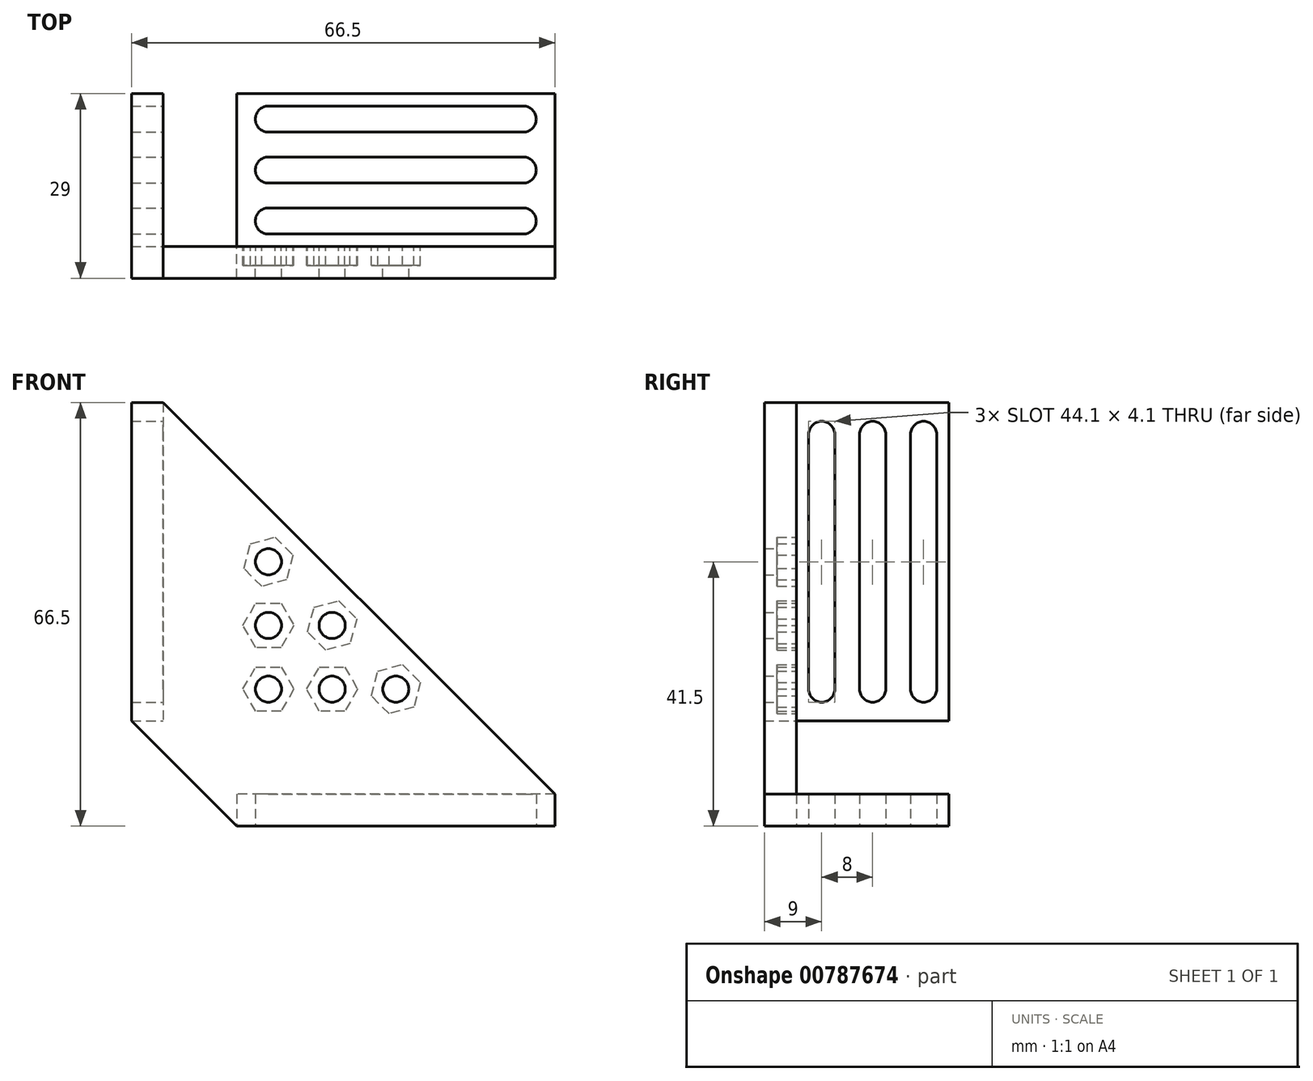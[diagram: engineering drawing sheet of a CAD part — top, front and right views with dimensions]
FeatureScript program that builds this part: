
annotation { "Feature Type Name" : "Feature", "Feature Type Description" : "" }
export const myFeature = defineFeature(function(context is Context, id is Id, definition is map)
    precondition{}
    {
        {
            var Q0;
            Q0=qCreatedBy(makeId("Top.planeOp"),FACE);
            var sketch = newSketch(context, id + "F0", { "sketchPlane" : qUnion([Q0])});
            skLineSegment(sketch, "E0.left", {"start": v(-21, 12) * mm, "end": v(-21, -12) * mm});
            skPoint(sketch, "E0.middle", {"position": v(0, 0) * mm});
            skLineSegment(sketch, "E1", {"start": v(-16, 12) * mm, "end": v(-16, -12) * mm, "construction": true});
            skPoint(sketch, "E2", {"position": v(-16, -8) * mm});
            skPoint(sketch, "E3", {"position": v(0, -8) * mm});
            skPoint(sketch, "E4", {"position": v(-16, 0) * mm});
            skArc(sketch, "E5", {"start": v(-16, -5.95) * mm, "mid": v(-18.05, -8) * mm, "end": v(-16, -10.05) * mm});
            skLineSegment(sketch, "E6", {"start": v(-16, -5.95) * mm, "end": v(0, -5.95) * mm});
            skLineSegment(sketch, "E7.MirrorCS", {"start": v(-16, -10.05) * mm, "end": v(0, -10.05) * mm});
            skArc(sketch, "E8", {"start": v(-16, -2.05) * mm, "mid": v(-18.05, 0) * mm, "end": v(-16, 2.05) * mm});
            skLineSegment(sketch, "E9", {"start": v(-16, -2.05) * mm, "end": v(0, -2.05) * mm});
            skPoint(sketch, "E10.MirrorP", {"position": v(-16, 2.05) * mm});
            skLineSegment(sketch, "E11.MirrorCS", {"start": v(-16, 2.05) * mm, "end": v(0, 2.05) * mm});
            skLineSegment(sketch, "E12.MirrorCS", {"start": v(0, -12) * mm, "end": v(0, 12) * mm, "construction": true});
            skLineSegment(sketch, "E13", {"start": v(-21, -12) * mm, "end": v(0, -12) * mm});
            skLineSegment(sketch, "E14", {"start": v(-21, 0) * mm, "end": v(0, 0) * mm, "construction": true});
            skLineSegment(sketch, "E15", {"start": v(0, -8) * mm, "end": v(-21, -8) * mm, "construction": true});
            skPoint(sketch, "E15.endSnap0", {"position": v(-18.05, -8) * mm});
            skLineSegment(sketch, "E16", {"start": v(0, -12) * mm, "end": v(29, -12) * mm});
            skLineSegment(sketch, "E17", {"start": v(29, -12) * mm, "end": v(29, 12) * mm});
            skLineSegment(sketch, "E18", {"start": v(29, 12) * mm, "end": v(-21, 12) * mm});
            skLineSegment(sketch, "E19", {"start": v(24, 12) * mm, "end": v(24, -12) * mm, "construction": true});
            skLineSegment(sketch, "E20", {"start": v(0, -5.95) * mm, "end": v(24, -5.95) * mm});
            skLineSegment(sketch, "E21", {"start": v(0, -10.05) * mm, "end": v(24, -10.05) * mm});
            skLineSegment(sketch, "E22", {"start": v(0, -2.05) * mm, "end": v(24, -2.05) * mm});
            skLineSegment(sketch, "E23", {"start": v(0, 2.05) * mm, "end": v(24, 2.05) * mm});
            skLineSegment(sketch, "E24", {"start": v(24, 0) * mm, "end": v(0, 0) * mm, "construction": true});
            skLineSegment(sketch, "E25", {"start": v(0, -8) * mm, "end": v(24, -8) * mm, "construction": true});
            skArc(sketch, "E26", {"start": v(24, -2.05) * mm, "mid": v(26.05, 0) * mm, "end": v(24, 2.05) * mm});
            skArc(sketch, "E27", {"start": v(24, -10.05) * mm, "mid": v(26.05, -8) * mm, "end": v(24, -5.95) * mm});
            skLineSegment(sketch, "E28.MirrorCS", {"start": v(0, 5.95) * mm, "end": v(24, 5.95) * mm});
            skLineSegment(sketch, "E29.MirrorCS", {"start": v(0, 10.05) * mm, "end": v(24, 10.05) * mm});
            skLineSegment(sketch, "E30.MirrorCS", {"start": v(-16, 10.05) * mm, "end": v(0, 10.05) * mm});
            skLineSegment(sketch, "E31.MirrorCS", {"start": v(-16, 5.95) * mm, "end": v(0, 5.95) * mm});
            skArc(sketch, "E32.MirrorCS", {"start": v(-16, 5.95) * mm, "mid": v(-18.05, 8) * mm, "end": v(-16, 10.05) * mm});
            skArc(sketch, "E33.MirrorCS", {"start": v(24, 10.05) * mm, "mid": v(26.05, 8) * mm, "end": v(24, 5.95) * mm});
            skSolve(sketch);
        }
        {
            var Q0;
            Q0=makeQuery(id+"F0.imprint","IMPRINT",FACE,{"disambiguationData":[TD([[makeQuery(id+"F0.imprint","IMPRINT",EDGE,{"derivedFrom":sQuery(id+"F0.wireOp",EDGE,"E0.bottom")}),-1.0]])]});
            var Q1;
            Q1=makeQuery(id+"F0.imprint","IMPRINT",FACE,{"disambiguationData":[TD([[makeQuery(id+"F0.imprint","IMPRINT",EDGE,{"derivedFrom":sQuery(id+"F0.wireOp",EDGE,"E0.left")}),1.0]])]});
            extrude(context, id + "F1", {"entities" : qUnion([Q0, Q1]), "depth" : 5 * mm, "offsetDistance" : 25 * mm});
        }
        {
            var Q0;
            Q0=makeQuery(id+"F1.opExtrude","SWEPT_FACE",FACE,{"disambiguationData":[OSD([sQuery(id+"F0.wireOp",EDGE,"E0.left")])]});
            var sketch = newSketch(context, id + "F2", { "sketchPlane" : qUnion([Q0])});
            skLineSegment(sketch, "E34", {"start": v(-12, 2.5) * mm, "end": v(12, 2.5) * mm, "construction": true});
            skSolve(sketch);
        }
        {
            var Q0;
            Q0=makeQuery(id+"F1.opExtrude","SWEPT_BODY",BODY,{"disambiguationData":[OSD([sQuery(id+"F0.wireOp",EDGE,"E0.bottom"),sQuery(id+"F0.wireOp",EDGE,"E0.top"),sQuery(id+"F0.wireOp",EDGE,"E0.left"),sQuery(id+"F0.wireOp",EDGE,"E0.right"),sQuery(id+"F0.wireOp",EDGE,"rf366HtQ-3S43-huQP-rZQL-GLvETnePYKPt"),sQuery(id+"F0.wireOp",EDGE,"72d57c59-205e-4b86-9b7f-fefa83471a3c0.MirrorC"),sQuery(id+"F0.wireOp",EDGE,"3BxVGwLA-TLUy-tZVP-cH0U-NxRYkcQ5ksQi"),sQuery(id+"F0.wireOp",EDGE,"b526d6a5-a937-4610-9a53-f8e406b30c9d0.MirrorC"),sQuery(id+"F0.wireOp",EDGE,"71981b63-6e51-433c-862b-60b74b25135c0.MirrorC"),sQuery(id+"F0.wireOp",EDGE,"b5f8f83e-67df-48da-9f18-6f8bbd20fa1b0.MirrorC"),sQuery(id+"F0.wireOp",EDGE,"1DxgEhBs-8iCY-IMLj-HmtB-05ri525AO9wY"),sQuery(id+"F0.wireOp",EDGE,"NxLUD5A4-VjtB-lD8M-x3iM-VxBEk0lLSaKk"),sQuery(id+"F0.wireOp",EDGE,"3f1f5e11-1e70-4af8-87df-d7b5c765f6460.MirrorC")])]});
            var Q1;
            Q1=sQuery(id+"F2.wireOp",EDGE,"E34");
            transform(context, id + "F3", {"entities" : qUnion([Q0]), "transformType" : TransformType.ROTATION, "transformAxis" : qUnion([Q1]), "angle" : 90 * degree, "makeCopy" : true});
        }
        {
            var Q0;
            Q0=makeQuery(id+"F3.opPattern","COPY",BODY,{"derivedFrom":makeQuery(id+"F1.opExtrude","SWEPT_BODY",BODY,{"disambiguationData":[OSD([sQuery(id+"F0.wireOp",EDGE,"E0.bottom"),sQuery(id+"F0.wireOp",EDGE,"E0.top"),sQuery(id+"F0.wireOp",EDGE,"E0.left"),sQuery(id+"F0.wireOp",EDGE,"E0.right"),sQuery(id+"F0.wireOp",EDGE,"rf366HtQ-3S43-huQP-rZQL-GLvETnePYKPt"),sQuery(id+"F0.wireOp",EDGE,"72d57c59-205e-4b86-9b7f-fefa83471a3c0.MirrorC"),sQuery(id+"F0.wireOp",EDGE,"3BxVGwLA-TLUy-tZVP-cH0U-NxRYkcQ5ksQi"),sQuery(id+"F0.wireOp",EDGE,"b526d6a5-a937-4610-9a53-f8e406b30c9d0.MirrorC"),sQuery(id+"F0.wireOp",EDGE,"71981b63-6e51-433c-862b-60b74b25135c0.MirrorC"),sQuery(id+"F0.wireOp",EDGE,"b5f8f83e-67df-48da-9f18-6f8bbd20fa1b0.MirrorC"),sQuery(id+"F0.wireOp",EDGE,"1DxgEhBs-8iCY-IMLj-HmtB-05ri525AO9wY"),sQuery(id+"F0.wireOp",EDGE,"NxLUD5A4-VjtB-lD8M-x3iM-VxBEk0lLSaKk"),sQuery(id+"F0.wireOp",EDGE,"3f1f5e11-1e70-4af8-87df-d7b5c765f6460.MirrorC")])]}),"instanceName":"1"});
            var Q1;
            Q1=qCreatedBy(makeId("Top.planeOp"),FACE);
            transform(context, id + "F4", {"entities" : qUnion([Q0]), "transformType" : TransformType.TRANSLATION_DISTANCE, "transformDirection" : qUnion([Q1]), "distance" : 14 * mm, "makeCopy" : false});
        }
        {
            var Q0;
            Q0=makeQuery(id+"F3.opPattern","COPY",BODY,{"derivedFrom":makeQuery(id+"F1.opExtrude","SWEPT_BODY",BODY,{"disambiguationData":[OSD([sQuery(id+"F0.wireOp",EDGE,"E0.bottom"),sQuery(id+"F0.wireOp",EDGE,"E0.top"),sQuery(id+"F0.wireOp",EDGE,"E0.left"),sQuery(id+"F0.wireOp",EDGE,"E0.right"),sQuery(id+"F0.wireOp",EDGE,"rf366HtQ-3S43-huQP-rZQL-GLvETnePYKPt"),sQuery(id+"F0.wireOp",EDGE,"72d57c59-205e-4b86-9b7f-fefa83471a3c0.MirrorC"),sQuery(id+"F0.wireOp",EDGE,"3BxVGwLA-TLUy-tZVP-cH0U-NxRYkcQ5ksQi"),sQuery(id+"F0.wireOp",EDGE,"b526d6a5-a937-4610-9a53-f8e406b30c9d0.MirrorC"),sQuery(id+"F0.wireOp",EDGE,"71981b63-6e51-433c-862b-60b74b25135c0.MirrorC"),sQuery(id+"F0.wireOp",EDGE,"b5f8f83e-67df-48da-9f18-6f8bbd20fa1b0.MirrorC"),sQuery(id+"F0.wireOp",EDGE,"1DxgEhBs-8iCY-IMLj-HmtB-05ri525AO9wY"),sQuery(id+"F0.wireOp",EDGE,"NxLUD5A4-VjtB-lD8M-x3iM-VxBEk0lLSaKk"),sQuery(id+"F0.wireOp",EDGE,"3f1f5e11-1e70-4af8-87df-d7b5c765f6460.MirrorC")])]}),"instanceName":"1"});
            var Q1;
            Q1=qCreatedBy(makeId("Right.planeOp"),FACE);
            transform(context, id + "F5", {"entities" : qUnion([Q0]), "transformType" : TransformType.TRANSLATION_DISTANCE, "transformDirection" : qUnion([Q1]), "distance" : 14 * mm, "oppositeDirection" : true, "makeCopy" : false});
        }
        {
            var Q0;
            Q0=makeQuery(id+"F3.opPattern","COPY",VERTEX,{"derivedFrom":makeQuery(id+"F1.opExtrude","CAP_VERTEX",VERTEX,{"disambiguationData":[OSD([sQuery(id+"F0.wireOp",EDGE,"E0.left"),sQuery(id+"F0.wireOp",EDGE,"E13")])],"isStart":false}),"instanceName":"1"});
            var Q1;
            Q1=makeQuery(id+"F3.opPattern","COPY",VERTEX,{"derivedFrom":makeQuery(id+"F1.opExtrude","CAP_VERTEX",VERTEX,{"disambiguationData":[OSD([sQuery(id+"F0.wireOp",EDGE,"E0.left"),sQuery(id+"F0.wireOp",EDGE,"E13")])],"isStart":true}),"instanceName":"1"});
            var Q2;
            Q2=sQuery(id+"F0.wireOp",VERTEX,"E0.left.end");
            cPlane(context, id + "F6", {"entities" : qUnion([Q0, Q1, Q2]), "cplaneType" : CPlaneType.THREE_POINT, "offset" : 25 * mm, "width" : 150 * mm, "height" : 150 * mm});
        }
        {
            var Q0;
            Q0=qCreatedBy(id+"F6.planeOp",FACE);
            var sketch = newSketch(context, id + "F7", { "sketchPlane" : qUnion([Q0])});
            skLineSegment(sketch, "E35", {"start": v(-21, 0) * mm, "end": v(-37.5, 16.5) * mm});
            skLineSegment(sketch, "E36", {"start": v(-32.5, 66.5) * mm, "end": v(29, 5) * mm});
            skLineSegment(sketch, "E37", {"start": v(-37.5, 16.5) * mm, "end": v(-37.5, 66.5) * mm});
            skLineSegment(sketch, "E38", {"start": v(-37.5, 66.5) * mm, "end": v(-32.5, 66.5) * mm});
            skLineSegment(sketch, "E39", {"start": v(-21, 0) * mm, "end": v(29, 0) * mm});
            skLineSegment(sketch, "E40", {"start": v(29, 0) * mm, "end": v(29, 5) * mm});
            skLineSegment(sketch, "E41", {"start": v(-32.5, 66.5) * mm, "end": v(-37.5, 66.5) * mm});
            skPoint(sketch, "E42", {"position": v(-6, 31.5) * mm});
            skCircle(sketch, "E43", {"center": v(-6, 31.5) * mm, "radius": 2.05 * mm});
            skCircle(sketch, "E44.cCircle", {"center": v(-6, 31.5) * mm, "radius": 4 * mm, "construction": true});
            skLineSegment(sketch, "E44.0", {"start": v(-8.82, 34.34) * mm, "end": v(-4.96, 35.37) * mm});
            skLineSegment(sketch, "E44.1", {"start": v(-4.96, 35.37) * mm, "end": v(-2.13, 32.54) * mm});
            skLineSegment(sketch, "E44.2", {"start": v(-2.13, 32.54) * mm, "end": v(-3.16, 28.68) * mm});
            skLineSegment(sketch, "E44.3", {"start": v(-3.16, 28.68) * mm, "end": v(-7.03, 27.64) * mm});
            skLineSegment(sketch, "E44.4", {"start": v(-7.03, 27.64) * mm, "end": v(-9.86, 30.47) * mm});
            skLineSegment(sketch, "E44.5", {"start": v(-9.86, 30.47) * mm, "end": v(-8.82, 34.34) * mm});
            skLineSegment(sketch, "E45", {"start": v(-29.25, 8.25) * mm, "end": v(-1.75, 35.75) * mm, "construction": true});
            skLineSegment(sketch, "E46", {"start": v(-37.5, 16.5) * mm, "end": v(-37.5, 0) * mm, "construction": true});
            skLineSegment(sketch, "E47", {"start": v(-37.5, 0) * mm, "end": v(-21, 0) * mm, "construction": true});
            skLineSegment(sketch, "E48", {"start": v(-21, 5) * mm, "end": v(-32.5, 5) * mm, "construction": true});
            skLineSegment(sketch, "E49", {"start": v(-32.5, 5) * mm, "end": v(-32.5, 16.5) * mm, "construction": true});
            skLineSegment(sketch, "E50", {"start": v(-24.5, 58.5) * mm, "end": v(-24.5, 13) * mm, "construction": true});
            skLineSegment(sketch, "E51", {"start": v(-24.5, 13) * mm, "end": v(21, 13) * mm, "construction": true});
            skPoint(sketch, "E52", {"position": v(-3.16, 34.34) * mm});
            skLineSegment(sketch, "E53", {"start": v(-6, 31.5) * mm, "end": v(-6, 13) * mm, "construction": true});
            skLineSegment(sketch, "E54", {"start": v(-6, 31.5) * mm, "end": v(-24.5, 31.5) * mm, "construction": true});
            skPoint(sketch, "E55", {"position": v(-6, 21.5) * mm});
            skCircle(sketch, "E56", {"center": v(-6, 21.5) * mm, "radius": 2.05 * mm});
            skCircle(sketch, "E57.cCircle", {"center": v(-6, 21.5) * mm, "radius": 4 * mm, "construction": true});
            skLineSegment(sketch, "E57.0", {"start": v(-8, 24.97) * mm, "end": v(-4, 24.97) * mm});
            skLineSegment(sketch, "E57.1", {"start": v(-4, 24.97) * mm, "end": v(-2, 21.5) * mm});
            skLineSegment(sketch, "E57.2", {"start": v(-2, 21.5) * mm, "end": v(-4, 18.04) * mm});
            skLineSegment(sketch, "E57.3", {"start": v(-4, 18.04) * mm, "end": v(-8, 18.04) * mm});
            skLineSegment(sketch, "E57.4", {"start": v(-8, 18.04) * mm, "end": v(-10, 21.5) * mm});
            skLineSegment(sketch, "E57.5", {"start": v(-10, 21.5) * mm, "end": v(-8, 24.97) * mm});
            skPoint(sketch, "E58", {"position": v(-16, 31.5) * mm});
            skCircle(sketch, "E59", {"center": v(-16, 31.5) * mm, "radius": 2.05 * mm});
            skCircle(sketch, "E60.cCircle", {"center": v(-16, 31.5) * mm, "radius": 4 * mm, "construction": true});
            skLineSegment(sketch, "E60.0", {"start": v(-18, 34.97) * mm, "end": v(-14, 34.97) * mm});
            skLineSegment(sketch, "E60.1", {"start": v(-14, 34.97) * mm, "end": v(-12, 31.5) * mm});
            skLineSegment(sketch, "E60.2", {"start": v(-12, 31.5) * mm, "end": v(-14, 28.04) * mm});
            skLineSegment(sketch, "E60.3", {"start": v(-14, 28.04) * mm, "end": v(-18, 28.04) * mm});
            skLineSegment(sketch, "E60.4", {"start": v(-18, 28.04) * mm, "end": v(-20, 31.5) * mm});
            skLineSegment(sketch, "E60.5", {"start": v(-20, 31.5) * mm, "end": v(-18, 34.97) * mm});
            skPoint(sketch, "E61", {"position": v(-16, 21.5) * mm});
            skCircle(sketch, "E62", {"center": v(-16, 21.5) * mm, "radius": 2.05 * mm});
            skCircle(sketch, "E63.cCircle", {"center": v(-16, 21.5) * mm, "radius": 4 * mm, "construction": true});
            skLineSegment(sketch, "E63.0", {"start": v(-18, 24.97) * mm, "end": v(-14, 24.97) * mm});
            skLineSegment(sketch, "E63.1", {"start": v(-14, 24.97) * mm, "end": v(-12, 21.5) * mm});
            skLineSegment(sketch, "E63.2", {"start": v(-12, 21.5) * mm, "end": v(-14, 18.04) * mm});
            skLineSegment(sketch, "E63.3", {"start": v(-14, 18.04) * mm, "end": v(-18, 18.04) * mm});
            skLineSegment(sketch, "E63.4", {"start": v(-18, 18.04) * mm, "end": v(-20, 21.5) * mm});
            skLineSegment(sketch, "E63.5", {"start": v(-20, 21.5) * mm, "end": v(-18, 24.97) * mm});
            skLineSegment(sketch, "E64", {"start": v(-6, 21.5) * mm, "end": v(12.5, 21.5) * mm, "construction": true});
            skLineSegment(sketch, "E65", {"start": v(-16, 31.5) * mm, "end": v(-16, 50) * mm, "construction": true});
            skPoint(sketch, "E66", {"position": v(4, 21.5) * mm});
            skCircle(sketch, "E67", {"center": v(4, 21.5) * mm, "radius": 2.05 * mm});
            skCircle(sketch, "E68.cCircle", {"center": v(4, 21.5) * mm, "radius": 4 * mm, "construction": true});
            skLineSegment(sketch, "E68.0", {"start": v(1.18, 24.34) * mm, "end": v(5.04, 25.37) * mm});
            skLineSegment(sketch, "E68.1", {"start": v(5.04, 25.37) * mm, "end": v(7.87, 22.54) * mm});
            skLineSegment(sketch, "E68.2", {"start": v(7.87, 22.54) * mm, "end": v(6.84, 18.68) * mm});
            skLineSegment(sketch, "E68.3", {"start": v(6.84, 18.68) * mm, "end": v(2.97, 17.64) * mm});
            skLineSegment(sketch, "E68.4", {"start": v(2.97, 17.64) * mm, "end": v(0.14, 20.47) * mm});
            skLineSegment(sketch, "E68.5", {"start": v(0.14, 20.47) * mm, "end": v(1.18, 24.34) * mm});
            skPoint(sketch, "E69", {"position": v(-16, 41.5) * mm});
            skCircle(sketch, "E70", {"center": v(-16, 41.5) * mm, "radius": 2.05 * mm});
            skCircle(sketch, "E71.cCircle", {"center": v(-16, 41.5) * mm, "radius": 4 * mm, "construction": true});
            skLineSegment(sketch, "E71.0", {"start": v(-18.82, 44.34) * mm, "end": v(-14.96, 45.37) * mm});
            skLineSegment(sketch, "E71.1", {"start": v(-14.96, 45.37) * mm, "end": v(-12.13, 42.54) * mm});
            skLineSegment(sketch, "E71.2", {"start": v(-12.13, 42.54) * mm, "end": v(-13.16, 38.68) * mm});
            skLineSegment(sketch, "E71.3", {"start": v(-13.16, 38.68) * mm, "end": v(-17.03, 37.64) * mm});
            skLineSegment(sketch, "E71.4", {"start": v(-17.03, 37.64) * mm, "end": v(-19.86, 40.47) * mm});
            skLineSegment(sketch, "E71.5", {"start": v(-19.86, 40.47) * mm, "end": v(-18.82, 44.34) * mm});
            skPoint(sketch, "E72", {"position": v(-13.16, 44.34) * mm});
            skSolve(sketch);
        }
        {
            var Q0;
            Q0=makeQuery(id+"F7.imprint","IMPRINT",FACE,{"disambiguationData":[TD([[makeQuery(id+"F7.imprint","IMPRINT",EDGE,{"derivedFrom":sQuery(id+"F7.wireOp",EDGE,"E36")}),-1.0]])]});
            var Q1;
            Q1=makeQuery(id+"F7.imprint","IMPRINT",FACE,{"disambiguationData":[TD([[makeQuery(id+"F7.imprint","IMPRINT",EDGE,{"derivedFrom":sQuery(id+"F7.wireOp",EDGE,"544cc5c5-56e9-462e-aa7d-0e891712fb88")}),-1.0]])]});
            var Q2;
            Q2=makeQuery(id+"F7.imprint","IMPRINT",FACE,{"disambiguationData":[TD([[makeQuery(id+"F7.imprint","IMPRINT",EDGE,{"derivedFrom":sQuery(id+"F7.wireOp",EDGE,"af930993-f983-4d4b-806c-d5d714f01deb")}),-1.0]])]});
            var Q3;
            Q3=makeQuery(id+"F7.imprint","IMPRINT",FACE,{"disambiguationData":[TD([[makeQuery(id+"F7.imprint","IMPRINT",EDGE,{"derivedFrom":sQuery(id+"F7.wireOp",EDGE,"E43")}),-1.0]])]});
            var Q4;
            Q4=makeQuery(id+"F7.imprint","IMPRINT",FACE,{"disambiguationData":[TD([[makeQuery(id+"F7.imprint","IMPRINT",EDGE,{"derivedFrom":sQuery(id+"F7.wireOp",EDGE,"db4000d2-28b7-4ce0-b6f8-efe2c8e47721")}),-1.0]])]});
            var Q5;
            Q5=makeQuery(id+"F7.imprint","IMPRINT",FACE,{"disambiguationData":[TD([[makeQuery(id+"F7.imprint","IMPRINT",EDGE,{"derivedFrom":sQuery(id+"F7.wireOp",EDGE,"6fd45c98-9014-41e2-a4b9-07c20c1fc8f4")}),-1.0]])]});
            var Q6;
            {var subQ0=sQuery(id+"F7.wireOp",EDGE,"36f95dd1-a930-4b05-802e-2328d4aa170c.1");Q6=makeQuery(id+"F7.imprint","IMPRINT",FACE,{"disambiguationData":[TD([[makeQuery(id+"F7.imprint","IMPRINT",EDGE,{"derivedFrom":subQ0}),-1.0]])]});}
            var Q7;
            Q7=makeQuery(id+"F7.imprint","IMPRINT",FACE,{"disambiguationData":[TD([[makeQuery(id+"F7.imprint","IMPRINT",EDGE,{"derivedFrom":sQuery(id+"F7.wireOp",EDGE,"0217be3f-f015-4376-87de-3fac7a7125e00.MirrorCS")}),1.0]])]});
            var Q8;
            Q8=makeQuery(id+"F7.imprint","IMPRINT",FACE,{"disambiguationData":[TD([[makeQuery(id+"F7.imprint","IMPRINT",EDGE,{"derivedFrom":sQuery(id+"F7.wireOp",EDGE,"3a05cbfe-0b2f-41ad-9fce-b7c3e8f461170.MirrorCS")}),1.0]])]});
            var Q9;
            Q9=makeQuery(id+"F7.imprint","IMPRINT",FACE,{"disambiguationData":[TD([[makeQuery(id+"F7.imprint","IMPRINT",EDGE,{"derivedFrom":sQuery(id+"F7.wireOp",EDGE,"686798c7-8504-4800-9966-571d6854760d0.MirrorCS")}),1.0]])]});
            var Q10;
            Q10=makeQuery(id+"F7.imprint","IMPRINT",FACE,{"disambiguationData":[TD([[makeQuery(id+"F7.imprint","IMPRINT",EDGE,{"derivedFrom":sQuery(id+"F7.wireOp",EDGE,"ee1293b9-60a1-4feb-baa6-848b5ec06ea80.MirrorCS")}),1.0]])]});
            var Q11;
            Q11=makeQuery(id+"F7.imprint","IMPRINT",FACE,{"disambiguationData":[TD([[makeQuery(id+"F7.imprint","IMPRINT",EDGE,{"derivedFrom":sQuery(id+"F7.wireOp",EDGE,"E70")}),-1.0]])]});
            var Q12;
            Q12=makeQuery(id+"F7.imprint","IMPRINT",FACE,{"disambiguationData":[TD([[makeQuery(id+"F7.imprint","IMPRINT",EDGE,{"derivedFrom":sQuery(id+"F7.wireOp",EDGE,"E59")}),-1.0]])]});
            var Q13;
            Q13=makeQuery(id+"F7.imprint","IMPRINT",FACE,{"disambiguationData":[TD([[makeQuery(id+"F7.imprint","IMPRINT",EDGE,{"derivedFrom":sQuery(id+"F7.wireOp",EDGE,"E62")}),-1.0]])]});
            var Q14;
            Q14=makeQuery(id+"F7.imprint","IMPRINT",FACE,{"disambiguationData":[TD([[makeQuery(id+"F7.imprint","IMPRINT",EDGE,{"derivedFrom":sQuery(id+"F7.wireOp",EDGE,"E56")}),-1.0]])]});
            var Q15;
            Q15=makeQuery(id+"F7.imprint","IMPRINT",FACE,{"disambiguationData":[TD([[makeQuery(id+"F7.imprint","IMPRINT",EDGE,{"derivedFrom":sQuery(id+"F7.wireOp",EDGE,"E67")}),-1.0]])]});
            extrude(context, id + "F8", {"entities" : qUnion([Q0, Q1, Q2, Q3, Q4, Q5, Q6, Q7, Q8, Q9, Q10, Q11, Q12, Q13, Q14, Q15]), "operationType" : NewBodyOperationType.ADD, "depth" : 5 * mm, "offsetDistance" : 25 * mm});
        }
        {
            var Q0;
            Q0=makeQuery(id+"F7.imprint","IMPRINT",FACE,{"disambiguationData":[TD([[makeQuery(id+"F7.imprint","IMPRINT",EDGE,{"derivedFrom":sQuery(id+"F7.wireOp",EDGE,"E43")}),-1.0]])]});
            var Q1;
            Q1=makeQuery(id+"F7.imprint","IMPRINT",FACE,{"disambiguationData":[TD([[makeQuery(id+"F7.imprint","IMPRINT",EDGE,{"derivedFrom":sQuery(id+"F7.wireOp",EDGE,"af930993-f983-4d4b-806c-d5d714f01deb")}),-1.0]])]});
            var Q2;
            Q2=makeQuery(id+"F7.imprint","IMPRINT",FACE,{"disambiguationData":[TD([[makeQuery(id+"F7.imprint","IMPRINT",EDGE,{"derivedFrom":sQuery(id+"F7.wireOp",EDGE,"544cc5c5-56e9-462e-aa7d-0e891712fb88")}),-1.0]])]});
            var Q3;
            Q3=makeQuery(id+"F7.imprint","IMPRINT",FACE,{"disambiguationData":[TD([[makeQuery(id+"F7.imprint","IMPRINT",EDGE,{"derivedFrom":sQuery(id+"F7.wireOp",EDGE,"a7fd36b7-951d-469d-bd4a-abdf8a5abec4")}),-1.0]])]});
            var Q4;
            Q4=makeQuery(id+"F7.imprint","IMPRINT",FACE,{"disambiguationData":[TD([[makeQuery(id+"F7.imprint","IMPRINT",EDGE,{"derivedFrom":sQuery(id+"F7.wireOp",EDGE,"db4000d2-28b7-4ce0-b6f8-efe2c8e47721")}),-1.0]])]});
            var Q5;
            Q5=makeQuery(id+"F7.imprint","IMPRINT",FACE,{"disambiguationData":[TD([[makeQuery(id+"F7.imprint","IMPRINT",EDGE,{"derivedFrom":sQuery(id+"F7.wireOp",EDGE,"6fd45c98-9014-41e2-a4b9-07c20c1fc8f4")}),-1.0]])]});
            var Q6;
            Q6=makeQuery(id+"F7.imprint","IMPRINT",FACE,{"disambiguationData":[TD([[makeQuery(id+"F7.imprint","IMPRINT",EDGE,{"derivedFrom":sQuery(id+"F7.wireOp",EDGE,"0217be3f-f015-4376-87de-3fac7a7125e00.MirrorCS")}),1.0]])]});
            var Q7;
            Q7=makeQuery(id+"F7.imprint","IMPRINT",FACE,{"disambiguationData":[TD([[makeQuery(id+"F7.imprint","IMPRINT",EDGE,{"derivedFrom":sQuery(id+"F7.wireOp",EDGE,"3a05cbfe-0b2f-41ad-9fce-b7c3e8f461170.MirrorCS")}),1.0]])]});
            var Q8;
            Q8=makeQuery(id+"F7.imprint","IMPRINT",FACE,{"disambiguationData":[TD([[makeQuery(id+"F7.imprint","IMPRINT",EDGE,{"derivedFrom":sQuery(id+"F7.wireOp",EDGE,"686798c7-8504-4800-9966-571d6854760d0.MirrorCS")}),1.0]])]});
            var Q9;
            Q9=makeQuery(id+"F7.imprint","IMPRINT",FACE,{"disambiguationData":[TD([[makeQuery(id+"F7.imprint","IMPRINT",EDGE,{"derivedFrom":sQuery(id+"F7.wireOp",EDGE,"ee1293b9-60a1-4feb-baa6-848b5ec06ea80.MirrorCS")}),1.0]])]});
            var Q10;
            Q10=makeQuery(id+"F7.imprint","IMPRINT",FACE,{"disambiguationData":[TD([[makeQuery(id+"F7.imprint","IMPRINT",EDGE,{"derivedFrom":sQuery(id+"F7.wireOp",EDGE,"E67")}),-1.0]])]});
            var Q11;
            Q11=makeQuery(id+"F7.imprint","IMPRINT",FACE,{"disambiguationData":[TD([[makeQuery(id+"F7.imprint","IMPRINT",EDGE,{"derivedFrom":sQuery(id+"F7.wireOp",EDGE,"E56")}),-1.0]])]});
            var Q12;
            Q12=makeQuery(id+"F7.imprint","IMPRINT",FACE,{"disambiguationData":[TD([[makeQuery(id+"F7.imprint","IMPRINT",EDGE,{"derivedFrom":sQuery(id+"F7.wireOp",EDGE,"E62")}),-1.0]])]});
            var Q13;
            Q13=makeQuery(id+"F7.imprint","IMPRINT",FACE,{"disambiguationData":[TD([[makeQuery(id+"F7.imprint","IMPRINT",EDGE,{"derivedFrom":sQuery(id+"F7.wireOp",EDGE,"E59")}),-1.0]])]});
            var Q14;
            Q14=makeQuery(id+"F7.imprint","IMPRINT",FACE,{"disambiguationData":[TD([[makeQuery(id+"F7.imprint","IMPRINT",EDGE,{"derivedFrom":sQuery(id+"F7.wireOp",EDGE,"E70")}),-1.0]])]});
            extrude(context, id + "F9", {"entities" : qUnion([Q0, Q1, Q2, Q3, Q4, Q5, Q6, Q7, Q8, Q9, Q10, Q11, Q12, Q13, Q14]), "operationType" : NewBodyOperationType.REMOVE, "depth" : 3 * mm, "offsetDistance" : 25 * mm});
        }
    });
